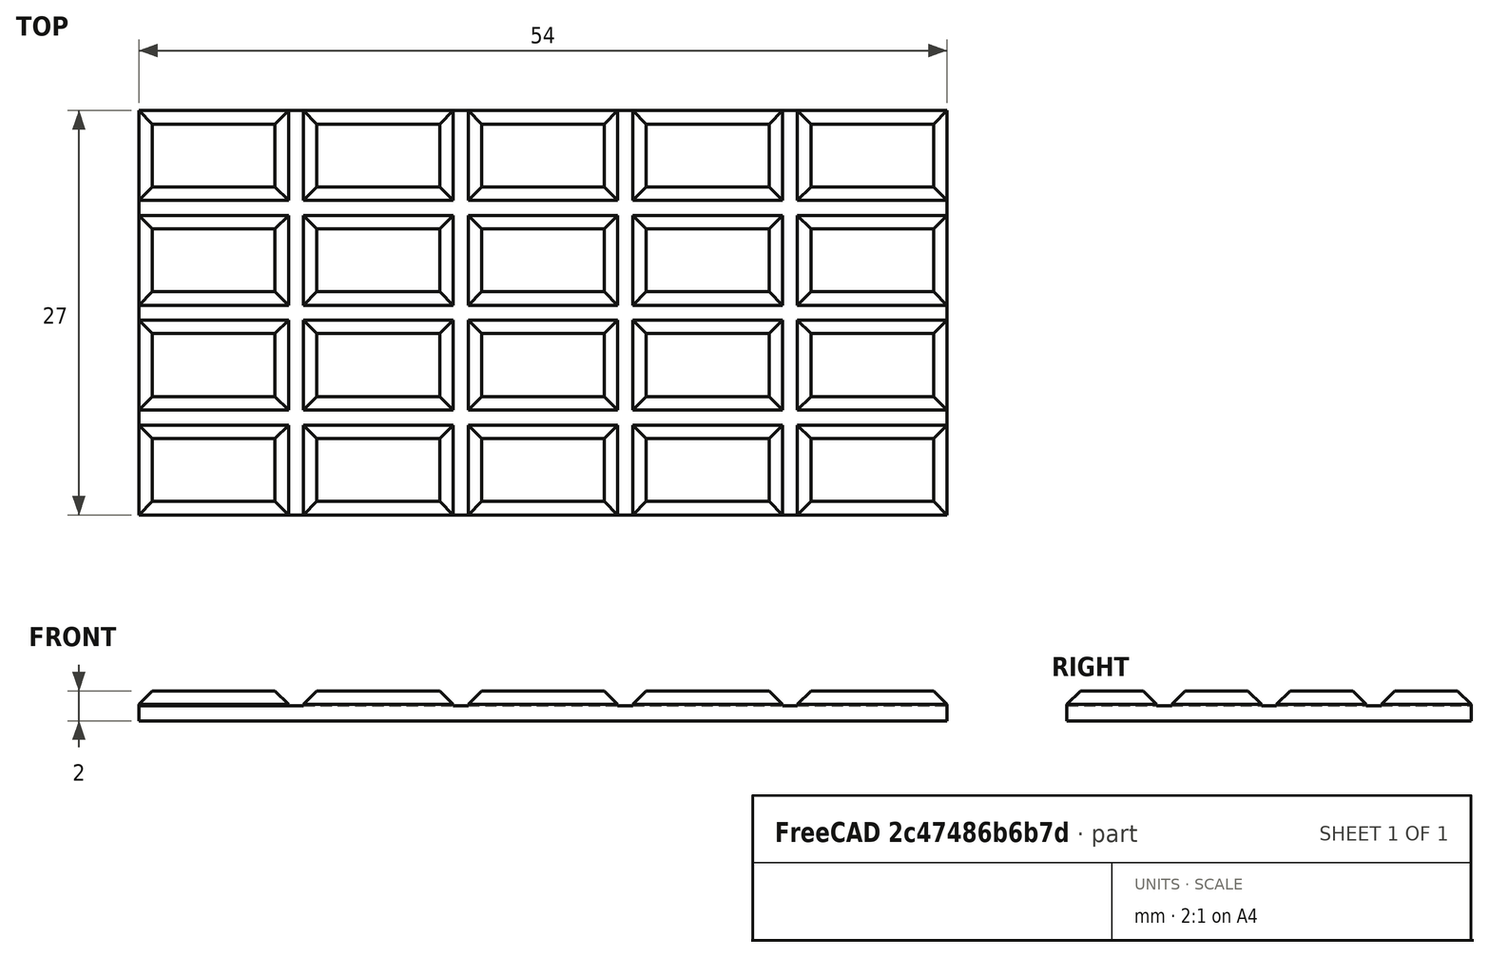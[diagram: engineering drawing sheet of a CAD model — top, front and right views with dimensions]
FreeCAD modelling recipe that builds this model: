
FCSTD DOCUMENT  (FreeCAD 1.0R39319 (Git))
Label: ojt1_t12r02_chocolat
License: All rights reserved
LicenseURL: https://en.wikipedia.org/wiki/All_rights_reserved
objects: Part::Box×2, Part::Chamfer×1, Part::FeaturePython×1, Part::MultiFuse×1
note: 4 computed .brp shape members not serialized (recipe doc carries the construction recipe); baked Part::Feature solids carry a one-line shape summary decoded from their .brp

FEATURE [Part::Box] Box  label="Cube"
  AttacherType = Attacher::AttachEngine3D
  Height = 1
  Length = 54
  Width = 27
FEATURE [Part::Box] Box001  label="Cube001"
  AttacherType = Attacher::AttachEngine3D
  Height = 1
  Length = 10
  Placement = pos=(0,0,1) rot=(0,0,1;0rad)
  Width = 6
FEATURE [Part::Chamfer] Chamfer
  Base = -> Box001
  EdgeLinks = -> Box001 [Edge2,Edge6,Edge10,Edge12]
  Edges = 4 edges r=0.9: [Edge2,Edge6,Edge10,Edge12]
FEATURE [Part::FeaturePython] Array  # Draft array (typed FeaturePython)
  AlwaysSyncPlacement = false
  Angle = 360
  ArrayType = 0
  Axis = (0,0,1)
  Base = -> Chamfer
  Center = (0,0,0)
  Count = 20
  ExpandArray = false
  Fuse = false
  IntervalAxis = (0,0,0)
  IntervalX = (11,0,0)
  IntervalY = (0,7,0)
  IntervalZ = (0,0,100)
  NumberCircles = 3
  NumberPolar = 5
  NumberX = 5
  NumberY = 4
  NumberZ = 1
  PlacementList = 20 placements: [(0,0,0),(0,7,0),(0,14,0),(0,21,0),(11,0,0),(11,7,0),(11,14,0),(11,21,0),(22,0,0),(22,7,0),(22,14,0),(22,21,0),(33,0,0),(33,7,0),(33,14,0),(33,21,0),(44,0,0),(44,7,0),(44,14,0),(44,21,0)]
  RadialDistance = 50
  ScaleList = (20) [(1,1,1),(1,1,1),(1,1,1),(1,1,1),(1,1,1),(1,1,1),(1,1,1),(1,1,1),(1,1,1),(1,1,1),(1,1,1),(1,1,1),(1,1,1),(1,1,1),(1,1,1),(1,1,1),(1,1,1),(1,1,1),(1,1,1),(1,1,1)]
  Symmetry = 1
  TangentialDistance = 25
FEATURE [Part::MultiFuse] Fusion
  Refine = true
  Shapes = -> [Box,Array]
